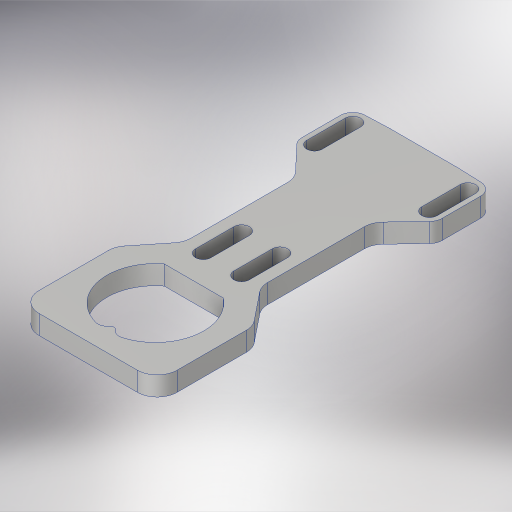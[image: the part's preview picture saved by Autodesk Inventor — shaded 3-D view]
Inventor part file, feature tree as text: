
AUTODESK INVENTOR PART (.ipt)
format: ipt  version: 2023.4 (Build 274418000, 418)  size: 718,336 bytes
history: native  units: in
note: dims shown in document units (in); Inventor stores cm internally (conversion verified against a paired STEP export)
features: extrude x8, sketch x7, other x7, fillet x6, projected_geometry x5
ambient origin geometry x8: Origin, YZ Plane, XZ Plane, XY Plane, X Axis, Y Axis, Z Axis, Center Point
bodies: Solid1 (feature_tree)
feature tree (33):
  sketch  "Sketch1"  dims[d1=0.7in d3=0.13in]
  extrude  "Extrusion1"  Depth=0.13in
  extrude  "Extrusion2"  Depth=0.197in
  extrude  "Extrusion3"  Depth=1.0in
  extrude  "Extrusion4"  Depth=0.25in
  fillet  "Fillet3"  Radius=0.25in
  extrude  "Extrusion5"  Depth=0.201in
  fillet  "Fillet4"  Radius=0.5in
  extrude  "Extrusion6"  Depth=0.5in
  extrude  "Extrusion7"  Depth=0.0625in
  fillet  "Fillet5"  Radius=0.5in
  other  "Full Round Fillet3"
  other  "Full Round Fillet4"
  other  "Full Round Fillet5"
  other  "Full Round Fillet6"
  other  "Full Round Fillet7"
  other  "Full Round Fillet8"
  other  "Full Round Fillet9"
  fillet  "Fillet6"  Radius=0.125in
  fillet  "Fillet8"  Radius=1.0in
  extrude  "Extrusion8"  Depth=0.0625in
  fillet  "Fillet7"  Radius=0.042in
  sketch  "Sketch2"  dims[d4=0.197in d5=0.197in]
  sketch  "Sketch3"  dims[d8=1.0in d9=3.0in]
  sketch  "Sketch4"  dims[d10=0.25in d11=0.5in d12=0.25in]
  sketch  "Sketch5"  dims[d13=0.25in d14=0.0in d23=0.201in d24=0.5in]
  sketch  "Sketch8"  dims[d26=2.3753in d27=0.5in]
  sketch  "Sketch9"  dims[d28=1.0in d29=0.0in d30=1.26in d31=0.5in d32=0.125in d33=1.0in d34=0.0in d36=0.093in d37=0.042in d38=1.0in d39=0.0in d40=0.125in d41=0.7874in d43=0.197in d44=0.3937in d46=1.0in d51=1.0in d52=0.0in d53=0.26in d54=1.5748in d56=0.197in d57=0.3937in d59=1.0in d61=1.8in d62=1.25in d64=1.75in d70=0.175in d71=0.0in d74=1.5in d75=0.06in d76=0.0in d77=0.13in d78=0.0625in d80=0.201in d81=1.5in d82=0.675in d83=0.5in d84=0.0625in d85=0.0625in d86=0.5in d87=0.06in d88=0.0in d89=0.26in d90=0.0625in]
  projected_geometry  "Project Cut Edges1"
  projected_geometry  "Project Cut Edges2"
  projected_geometry  "Project Cut Edges3"
  projected_geometry  "Project Cut Edges4"
  projected_geometry  "Project Cut Edges7"
